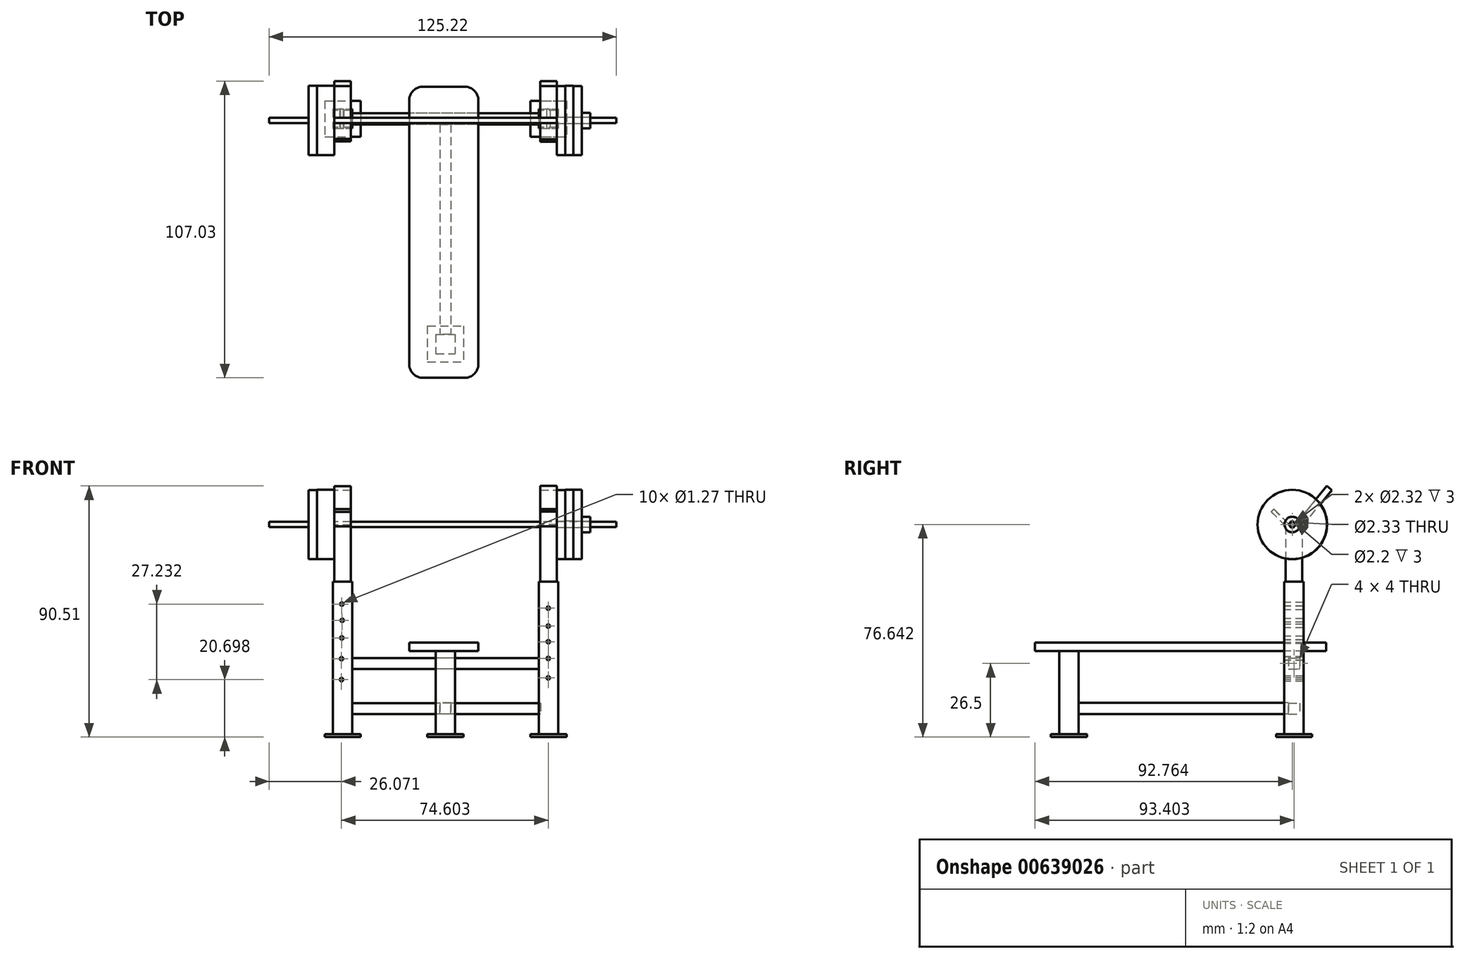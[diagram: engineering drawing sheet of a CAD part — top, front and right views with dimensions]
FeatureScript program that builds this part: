
annotation { "Feature Type Name" : "Feature", "Feature Type Description" : "" }
export const myFeature = defineFeature(function(context is Context, id is Id, definition is map)
    precondition{}
    {
        {
            var Q0;
            Q0=qCreatedBy(makeId("Top.planeOp"),FACE);
            var sketch = newSketch(context, id + "F0", { "sketchPlane" : qUnion([Q0])});
            skLineSegment(sketch, "E0.bottom", {"start": v(-45.73, 47.1) * mm, "end": v(-32.73, 47.1) * mm});
            skLineSegment(sketch, "E0.top", {"start": v(-45.73, 34.1) * mm, "end": v(-32.73, 34.1) * mm});
            skLineSegment(sketch, "E0.left", {"start": v(-45.73, 47.1) * mm, "end": v(-45.73, 34.1) * mm});
            skLineSegment(sketch, "E0.right", {"start": v(-32.73, 47.1) * mm, "end": v(-32.73, 34.1) * mm});
            skLineSegment(sketch, "E1.bottom", {"start": v(28.55, 47.1) * mm, "end": v(41.55, 47.1) * mm});
            skLineSegment(sketch, "E1.top", {"start": v(28.55, 34.1) * mm, "end": v(41.55, 34.1) * mm});
            skLineSegment(sketch, "E1.left", {"start": v(28.55, 47.1) * mm, "end": v(28.55, 34.1) * mm});
            skLineSegment(sketch, "E1.right", {"start": v(41.55, 47.1) * mm, "end": v(41.55, 34.1) * mm});
            skLineSegment(sketch, "E2.bottom", {"start": v(-8.67, -34.08) * mm, "end": v(4.33, -34.08) * mm});
            skLineSegment(sketch, "E2.top", {"start": v(-8.67, -47.08) * mm, "end": v(4.33, -47.08) * mm});
            skLineSegment(sketch, "E2.left", {"start": v(-8.67, -34.08) * mm, "end": v(-8.67, -47.08) * mm});
            skLineSegment(sketch, "E2.right", {"start": v(4.33, -34.08) * mm, "end": v(4.33, -47.08) * mm});
            skSolve(sketch);
        }
        {
            var Q0;
            Q0 = qSketchRegion(id + "F0", true);
            extrude(context, id + "F1", {"entities" : qUnion([Q0]), "depth" : 1 * mm, "offsetDistance" : 25.4 * mm});
        }
        {
            var Q0;
            Q0=makeQuery(id+"F1.opExtrude","CAP_FACE",FACE,{"disambiguationData":[OSD([sQuery(id+"F0.wireOp",EDGE,"E0.bottom"),sQuery(id+"F0.wireOp",EDGE,"E0.top"),sQuery(id+"F0.wireOp",EDGE,"E0.left"),sQuery(id+"F0.wireOp",EDGE,"E0.right")])],"isStart":false});
            var sketch = newSketch(context, id + "F2", { "sketchPlane" : qUnion([Q0])});
            skLineSegment(sketch, "E3.bottom", {"start": v(-42.73, 44.1) * mm, "end": v(-35.73, 44.1) * mm});
            skLineSegment(sketch, "E3.top", {"start": v(-42.73, 37.1) * mm, "end": v(-35.73, 37.1) * mm});
            skLineSegment(sketch, "E3.left", {"start": v(-42.73, 44.1) * mm, "end": v(-42.73, 37.1) * mm});
            skLineSegment(sketch, "E3.right", {"start": v(-35.73, 44.1) * mm, "end": v(-35.73, 37.1) * mm});
            skSolve(sketch);
        }
        {
            var Q0;
            Q0 = qSketchRegion(id + "F2", true);
            extrude(context, id + "F3", {"entities" : qUnion([Q0]), "operationType" : NewBodyOperationType.ADD, "depth" : 55 * mm, "offsetDistance" : 25.4 * mm});
        }
        {
            var Q0;
            Q0=makeQuery(id+"F1.opExtrude","CAP_FACE",FACE,{"disambiguationData":[OSD([sQuery(id+"F0.wireOp",EDGE,"E1.bottom"),sQuery(id+"F0.wireOp",EDGE,"E1.top"),sQuery(id+"F0.wireOp",EDGE,"E1.left"),sQuery(id+"F0.wireOp",EDGE,"E1.right")])],"isStart":false});
            var sketch = newSketch(context, id + "F4", { "sketchPlane" : qUnion([Q0])});
            skLineSegment(sketch, "E4.bottom", {"start": v(31.55, 44.1) * mm, "end": v(38.55, 44.1) * mm});
            skLineSegment(sketch, "E4.top", {"start": v(31.55, 37.1) * mm, "end": v(38.55, 37.1) * mm});
            skLineSegment(sketch, "E4.left", {"start": v(31.55, 44.1) * mm, "end": v(31.55, 37.1) * mm});
            skLineSegment(sketch, "E4.right", {"start": v(38.55, 44.1) * mm, "end": v(38.55, 37.1) * mm});
            skSolve(sketch);
        }
        {
            var Q0;
            Q0 = qSketchRegion(id + "F4", true);
            extrude(context, id + "F5", {"entities" : qUnion([Q0]), "operationType" : NewBodyOperationType.ADD, "depth" : 55 * mm, "offsetDistance" : 25.4 * mm});
        }
        {
            var Q0;
            Q0=makeQuery(id+"F1.opExtrude","CAP_FACE",FACE,{"disambiguationData":[OSD([sQuery(id+"F0.wireOp",EDGE,"E2.bottom"),sQuery(id+"F0.wireOp",EDGE,"E2.top"),sQuery(id+"F0.wireOp",EDGE,"E2.left"),sQuery(id+"F0.wireOp",EDGE,"E2.right")])],"isStart":false});
            var sketch = newSketch(context, id + "F6", { "sketchPlane" : qUnion([Q0])});
            skLineSegment(sketch, "E5.bottom", {"start": v(-5.67, -37.08) * mm, "end": v(1.33, -37.08) * mm});
            skLineSegment(sketch, "E5.top", {"start": v(-5.67, -44.08) * mm, "end": v(1.33, -44.08) * mm});
            skLineSegment(sketch, "E5.left", {"start": v(-5.67, -37.08) * mm, "end": v(-5.67, -44.08) * mm});
            skLineSegment(sketch, "E5.right", {"start": v(1.33, -37.08) * mm, "end": v(1.33, -44.08) * mm});
            skSolve(sketch);
        }
        {
            var Q0;
            Q0 = qSketchRegion(id + "F6", true);
            extrude(context, id + "F7", {"entities" : qUnion([Q0]), "operationType" : NewBodyOperationType.ADD, "depth" : 30 * mm, "offsetDistance" : 25.4 * mm});
        }
        {
            var Q0;
            Q0=makeQuery(id+"F3.opExtrude","SWEPT_FACE",FACE,{"disambiguationData":[OSD([sQuery(id+"F2.wireOp",EDGE,"E3.right")])]});
            var sketch = newSketch(context, id + "F8", { "sketchPlane" : qUnion([Q0])});
            skLineSegment(sketch, "E6.bottom", {"start": v(38.6, 12.27) * mm, "end": v(42.6, 12.27) * mm});
            skLineSegment(sketch, "E6.top", {"start": v(38.6, 8.27) * mm, "end": v(42.6, 8.27) * mm});
            skLineSegment(sketch, "E6.left", {"start": v(38.6, 12.27) * mm, "end": v(38.6, 8.27) * mm});
            skLineSegment(sketch, "E6.right", {"start": v(42.6, 12.27) * mm, "end": v(42.6, 8.27) * mm});
            skSolve(sketch);
        }
        {
            var Q0;
            Q0 = qSketchRegion(id + "F8", true);
            extrude(context, id + "F9", {"entities" : qUnion([Q0]), "depth" : 67.92 * mm, "offsetDistance" : 25.4 * mm});
        }
        {
            var Q0;
            Q0=makeQuery(id+"F3.opExtrude","SWEPT_FACE",FACE,{"disambiguationData":[OSD([sQuery(id+"F2.wireOp",EDGE,"E3.right")])]});
            var sketch = newSketch(context, id + "F10", { "sketchPlane" : qUnion([Q0])});
            skPoint(sketch, "E7.firstSnap0", {"position": v(37.1, 28.5) * mm});
            skLineSegment(sketch, "E7.bottom", {"start": v(38.6, 28.5) * mm, "end": v(42.6, 28.5) * mm});
            skLineSegment(sketch, "E7.top", {"start": v(38.6, 24.5) * mm, "end": v(42.6, 24.5) * mm});
            skLineSegment(sketch, "E7.left", {"start": v(38.6, 28.5) * mm, "end": v(38.6, 24.5) * mm});
            skLineSegment(sketch, "E7.right", {"start": v(42.6, 28.5) * mm, "end": v(42.6, 24.5) * mm});
            skSolve(sketch);
        }
        {
            var Q0;
            Q0 = qSketchRegion(id + "F10", true);
            extrude(context, id + "F11", {"entities" : qUnion([Q0]), "operationType" : NewBodyOperationType.ADD, "depth" : 67.82 * mm, "offsetDistance" : 25.4 * mm});
        }
        {
            var Q0;
            Q0=makeQuery(id+"F7.opExtrude","SWEPT_FACE",FACE,{"disambiguationData":[OSD([sQuery(id+"F6.wireOp",EDGE,"E5.bottom")])]});
            var sketch = newSketch(context, id + "F12", { "sketchPlane" : qUnion([Q0])});
            skLineSegment(sketch, "E8.bottom", {"start": v(0.17, 12.32) * mm, "end": v(4.17, 12.32) * mm});
            skLineSegment(sketch, "E8.top", {"start": v(0.17, 8.32) * mm, "end": v(4.17, 8.32) * mm});
            skLineSegment(sketch, "E8.left", {"start": v(0.17, 12.32) * mm, "end": v(0.17, 8.32) * mm});
            skLineSegment(sketch, "E8.right", {"start": v(4.17, 12.32) * mm, "end": v(4.17, 8.32) * mm});
            skSolve(sketch);
        }
        {
            var Q0;
            Q0 = qSketchRegion(id + "F12", true);
            extrude(context, id + "F13", {"entities" : qUnion([Q0]), "operationType" : NewBodyOperationType.ADD, "depth" : 75.72 * mm, "offsetDistance" : 25.4 * mm});
        }
        {
            var Q0;
            Q0=makeQuery(id+"F7.opExtrude","CAP_FACE",FACE,{"disambiguationData":[OSD([sQuery(id+"F6.wireOp",EDGE,"E5.bottom"),sQuery(id+"F6.wireOp",EDGE,"E5.top"),sQuery(id+"F6.wireOp",EDGE,"E5.left"),sQuery(id+"F6.wireOp",EDGE,"E5.right")])],"isStart":false});
            cPlane(context, id + "F14", {"entities" : qUnion([Q0]), "cplaneType" : CPlaneType.OFFSET, "offset" : 0 * mm, "width" : 152.4 * mm, "height" : 152.4 * mm});
        }
        {
            var Q0;
            Q0=qCreatedBy(id+"F14.planeOp",FACE);
            var sketch = newSketch(context, id + "F15", { "sketchPlane" : qUnion([Q0])});
            skLineSegment(sketch, "E9.bottom", {"start": v(9.77, 52.19) * mm, "end": v(-15.23, 52.19) * mm});
            skLineSegment(sketch, "E9.top", {"start": v(9.77, -52.81) * mm, "end": v(-15.23, -52.81) * mm});
            skLineSegment(sketch, "E9.left", {"start": v(9.77, 52.19) * mm, "end": v(9.77, -52.81) * mm});
            skLineSegment(sketch, "E9.right", {"start": v(-15.23, 52.19) * mm, "end": v(-15.23, -52.81) * mm});
            skSolve(sketch);
        }
        {
            var Q0;
            Q0 = qSketchRegion(id + "F15", true);
            extrude(context, id + "F16", {"entities" : qUnion([Q0]), "depth" : 3 * mm, "offsetDistance" : 25.4 * mm});
        }
        {
            var Q0;
            Q0=makeQuery(id+"F16.opExtrude","SWEPT_EDGE",EDGE,{"disambiguationData":[OSD([sQuery(id+"F15.wireOp",EDGE,"E9.bottom"),sQuery(id+"F15.wireOp",EDGE,"E9.right")])]});
            var Q1;
            Q1=makeQuery(id+"F16.opExtrude","SWEPT_EDGE",EDGE,{"disambiguationData":[OSD([sQuery(id+"F15.wireOp",EDGE,"E9.top"),sQuery(id+"F15.wireOp",EDGE,"E9.right")])]});
            var Q2;
            Q2=makeQuery(id+"F16.opExtrude","SWEPT_EDGE",EDGE,{"disambiguationData":[OSD([sQuery(id+"F15.wireOp",EDGE,"E9.top"),sQuery(id+"F15.wireOp",EDGE,"E9.left")])]});
            var Q3;
            Q3=makeQuery(id+"F16.opExtrude","SWEPT_EDGE",EDGE,{"disambiguationData":[OSD([sQuery(id+"F15.wireOp",EDGE,"E9.bottom"),sQuery(id+"F15.wireOp",EDGE,"E9.left")])]});
            fillet(context, id + "F17", {"entities" : qUnion([Q0, Q1, Q2, Q3]), "radius" : 5.08 * mm, "tangentPropagation" : true, "allowEdgeOverflow" : false});
        }
        {
            var Q0;
            Q0=makeQuery(id+"F3.opExtrude","CAP_FACE",FACE,{"disambiguationData":[OSD([sQuery(id+"F2.wireOp",EDGE,"E3.bottom"),sQuery(id+"F2.wireOp",EDGE,"E3.top"),sQuery(id+"F2.wireOp",EDGE,"E3.left"),sQuery(id+"F2.wireOp",EDGE,"E3.right")])],"isStart":false});
            var sketch = newSketch(context, id + "F18", { "sketchPlane" : qUnion([Q0])});
            skLineSegment(sketch, "E10.bottom", {"start": v(-36.23, 43.6) * mm, "end": v(-42.23, 43.6) * mm});
            skLineSegment(sketch, "E10.top", {"start": v(-36.23, 37.6) * mm, "end": v(-42.23, 37.6) * mm});
            skLineSegment(sketch, "E10.left", {"start": v(-36.23, 43.6) * mm, "end": v(-36.23, 37.6) * mm});
            skLineSegment(sketch, "E10.right", {"start": v(-42.23, 43.6) * mm, "end": v(-42.23, 37.6) * mm});
            skSolve(sketch);
        }
        {
            var Q0;
            Q0 = qSketchRegion(id + "F18", true);
            extrude(context, id + "F19", {"entities" : qUnion([Q0]), "operationType" : NewBodyOperationType.ADD, "depth" : 20 * mm, "offsetDistance" : 25.4 * mm});
        }
        {
            var Q0;
            Q0=makeQuery(id+"F5.opExtrude","CAP_FACE",FACE,{"disambiguationData":[OSD([sQuery(id+"F4.wireOp",EDGE,"E4.bottom"),sQuery(id+"F4.wireOp",EDGE,"E4.top"),sQuery(id+"F4.wireOp",EDGE,"E4.left"),sQuery(id+"F4.wireOp",EDGE,"E4.right")])],"isStart":false});
            var sketch = newSketch(context, id + "F20", { "sketchPlane" : qUnion([Q0])});
            skLineSegment(sketch, "E11.bottom", {"start": v(38.05, 37.6) * mm, "end": v(32.05, 37.6) * mm});
            skLineSegment(sketch, "E11.top", {"start": v(38.05, 43.6) * mm, "end": v(32.05, 43.6) * mm});
            skLineSegment(sketch, "E11.left", {"start": v(38.05, 37.6) * mm, "end": v(38.05, 43.6) * mm});
            skLineSegment(sketch, "E11.right", {"start": v(32.05, 37.6) * mm, "end": v(32.05, 43.6) * mm});
            skSolve(sketch);
        }
        {
            var Q0;
            Q0 = qSketchRegion(id + "F20", true);
            extrude(context, id + "F21", {"entities" : qUnion([Q0]), "operationType" : NewBodyOperationType.ADD, "depth" : 20 * mm, "offsetDistance" : 25.4 * mm});
        }
        {
            var Q0;
            Q0=makeQuery(id+"F21.opExtrude","SWEPT_FACE",FACE,{"disambiguationData":[OSD([sQuery(id+"F20.wireOp",EDGE,"E11.left")])]});
            var sketch = newSketch(context, id + "F22", { "sketchPlane" : qUnion([Q0])});
            skLineSegment(sketch, "E12", {"start": v(37.6, 76) * mm, "end": v(32.31, 81.3) * mm});
            skLineSegment(sketch, "E13", {"start": v(32.31, 81.3) * mm, "end": v(33.22, 82.2) * mm});
            skLineSegment(sketch, "E14", {"start": v(33.22, 82.2) * mm, "end": v(39.4, 76) * mm});
            skLineSegment(sketch, "E15", {"start": v(39.4, 76) * mm, "end": v(37.6, 76) * mm});
            skSolve(sketch);
        }
        {
            var Q0;
            Q0 = qSketchRegion(id + "F22", true);
            extrude(context, id + "F23", {"entities" : qUnion([Q0]), "operationType" : NewBodyOperationType.ADD, "oppositeDirection" : true, "depth" : 6 * mm, "offsetDistance" : 25.4 * mm});
        }
        {
            var Q0;
            Q0=makeQuery(id+"F23.boolean.opBoolean","MERGE",FACE,{"derivedFrom":[makeQuery(id+"F21.opExtrude","SWEPT_FACE",FACE,{"disambiguationData":[OSD([sQuery(id+"F20.wireOp",EDGE,"E11.left")])]}),makeQuery(id+"F23.opExtrude","CAP_FACE",FACE,{"disambiguationData":[OSD([sQuery(id+"F22.wireOp",EDGE,"E12"),sQuery(id+"F22.wireOp",EDGE,"E13"),sQuery(id+"F22.wireOp",EDGE,"E14"),sQuery(id+"F22.wireOp",EDGE,"E15")])],"isStart":true})]});
            var sketch = newSketch(context, id + "F24", { "sketchPlane" : qUnion([Q0])});
            skLineSegment(sketch, "E16", {"start": v(43.6, 76) * mm, "end": v(54.22, 89) * mm});
            skLineSegment(sketch, "E17", {"start": v(54.22, 89) * mm, "end": v(52.37, 90.5) * mm});
            skLineSegment(sketch, "E18", {"start": v(52.37, 90.5) * mm, "end": v(40.51, 76) * mm});
            skPoint(sketch, "E18.endSnap0", {"position": v(41.5, 76) * mm});
            skLineSegment(sketch, "E19", {"start": v(40.51, 76) * mm, "end": v(43.6, 76) * mm});
            skSolve(sketch);
        }
        {
            var Q0;
            Q0 = qSketchRegion(id + "F24", true);
            extrude(context, id + "F25", {"entities" : qUnion([Q0]), "operationType" : NewBodyOperationType.ADD, "oppositeDirection" : true, "depth" : 6 * mm, "offsetDistance" : 25.4 * mm});
        }
        {
            var Q0;
            Q0=makeQuery(id+"F19.opExtrude","SWEPT_FACE",FACE,{"disambiguationData":[OSD([sQuery(id+"F18.wireOp",EDGE,"E10.right")])]});
            var sketch = newSketch(context, id + "F26", { "sketchPlane" : qUnion([Q0])});
            skLineSegment(sketch, "E20", {"start": v(-37.6, 76) * mm, "end": v(-32.41, 81.17) * mm});
            skLineSegment(sketch, "E21", {"start": v(-32.41, 81.17) * mm, "end": v(-33.37, 82.13) * mm});
            skLineSegment(sketch, "E22", {"start": v(-33.37, 82.13) * mm, "end": v(-39.51, 76) * mm});
            skLineSegment(sketch, "E23", {"start": v(-39.51, 76) * mm, "end": v(-37.6, 76) * mm});
            skLineSegment(sketch, "E24", {"start": v(-43.6, 76) * mm, "end": v(-54.18, 88.94) * mm});
            skLineSegment(sketch, "E25", {"start": v(-54.18, 88.94) * mm, "end": v(-52.34, 90.44) * mm});
            skLineSegment(sketch, "E26", {"start": v(-52.34, 90.44) * mm, "end": v(-40.53, 76) * mm});
            skLineSegment(sketch, "E27", {"start": v(-40.53, 76) * mm, "end": v(-43.6, 76) * mm});
            skSolve(sketch);
        }
        {
            var Q0;
            Q0 = qSketchRegion(id + "F26", true);
            extrude(context, id + "F27", {"entities" : qUnion([Q0]), "operationType" : NewBodyOperationType.ADD, "oppositeDirection" : true, "depth" : 6 * mm, "offsetDistance" : 25.4 * mm});
        }
        {
            var Q0;
            Q0=makeQuery(id+"F27.boolean.opBoolean","MERGE",FACE,{"derivedFrom":[makeQuery(id+"F19.opExtrude","SWEPT_FACE",FACE,{"disambiguationData":[OSD([sQuery(id+"F18.wireOp",EDGE,"E10.right")])]}),makeQuery(id+"F27.opExtrude","CAP_FACE",FACE,{"disambiguationData":[OSD([sQuery(id+"F26.wireOp",EDGE,"E20"),sQuery(id+"F26.wireOp",EDGE,"E21"),sQuery(id+"F26.wireOp",EDGE,"E22"),sQuery(id+"F26.wireOp",EDGE,"E23")])],"isStart":true}),makeQuery(id+"F27.opExtrude","CAP_FACE",FACE,{"disambiguationData":[OSD([sQuery(id+"F26.wireOp",EDGE,"E24"),sQuery(id+"F26.wireOp",EDGE,"E25"),sQuery(id+"F26.wireOp",EDGE,"E26"),sQuery(id+"F26.wireOp",EDGE,"E27")])],"isStart":true})]});
            var sketch = newSketch(context, id + "F28", { "sketchPlane" : qUnion([Q0])});
            skCircle(sketch, "E28", {"center": v(-40.02, 76.62) * mm, "radius": 12.5 * mm});
            skPoint(sketch, "E28.centerSnap0", {"position": v(-40.02, 76) * mm});
            skSolve(sketch);
        }
        {
            var Q0;
            Q0 = qSketchRegion(id + "F28", true);
            extrude(context, id + "F29", {"entities" : qUnion([Q0]), "operationType" : NewBodyOperationType.ADD, "depth" : 3.17 * mm, "offsetDistance" : 25.4 * mm});
        }
        {
            var Q0;
            Q0=makeQuery(id+"F29.opExtrude","CAP_FACE",FACE,{"disambiguationData":[OSD([sQuery(id+"F28.wireOp",EDGE,"E28")])],"isStart":false});
            var sketch = newSketch(context, id + "F30", { "sketchPlane" : qUnion([Q0])});
            skCircle(sketch, "E29", {"center": v(-40.02, 76.62) * mm, "radius": 12.5 * mm});
            skSolve(sketch);
        }
        {
            var Q0;
            Q0 = qSketchRegion(id + "F30", true);
            extrude(context, id + "F31", {"entities" : qUnion([Q0]), "operationType" : NewBodyOperationType.ADD, "depth" : 3.05 * mm, "offsetDistance" : 25.4 * mm});
        }
        {
            var Q0;
            Q0=makeQuery(id+"F31.opExtrude","CAP_FACE",FACE,{"disambiguationData":[OSD([sQuery(id+"F30.wireOp",EDGE,"E29")])],"isStart":false});
            var sketch = newSketch(context, id + "F32", { "sketchPlane" : qUnion([Q0])});
            skCircle(sketch, "E30", {"center": v(-40.02, 76.62) * mm, "radius": 12.48 * mm});
            skSolve(sketch);
        }
        {
            var Q0;
            Q0 = qSketchRegion(id + "F32", true);
            extrude(context, id + "F33", {"entities" : qUnion([Q0]), "operationType" : NewBodyOperationType.ADD, "depth" : 3.05 * mm, "offsetDistance" : 25.4 * mm});
        }
        {
            var Q0;
            Q0=makeQuery(id+"F33.opExtrude","CAP_FACE",FACE,{"disambiguationData":[OSD([sQuery(id+"F32.wireOp",EDGE,"E30")])],"isStart":false});
            var sketch = newSketch(context, id + "F34", { "sketchPlane" : qUnion([Q0])});
            skCircle(sketch, "E31", {"center": v(-40.02, 76.62) * mm, "radius": 0.95 * mm});
            skSolve(sketch);
        }
        {
            var Q0;
            Q0 = qSketchRegion(id + "F34", true);
            extrude(context, id + "F35", {"entities" : qUnion([Q0]), "operationType" : NewBodyOperationType.ADD, "oppositeDirection" : true, "depth" : 111 * mm, "offsetDistance" : 25.4 * mm, "hasSecondDirection" : true, "secondDirectionOppositeDirection" : false, "secondDirectionDepth" : 14.22 * mm});
        }
        {
            var Q0;
            Q0=makeQuery(id+"F25.boolean.opBoolean","MERGE",FACE,{"derivedFrom":[makeQuery(id+"F23.boolean.opBoolean","MERGE",FACE,{"derivedFrom":[makeQuery(id+"F21.opExtrude","SWEPT_FACE",FACE,{"disambiguationData":[OSD([sQuery(id+"F20.wireOp",EDGE,"E11.left")])]}),makeQuery(id+"F23.opExtrude","CAP_FACE",FACE,{"disambiguationData":[OSD([sQuery(id+"F22.wireOp",EDGE,"E12"),sQuery(id+"F22.wireOp",EDGE,"E13"),sQuery(id+"F22.wireOp",EDGE,"E14"),sQuery(id+"F22.wireOp",EDGE,"E15")])],"isStart":true})]}),makeQuery(id+"F25.opExtrude","CAP_FACE",FACE,{"disambiguationData":[OSD([sQuery(id+"F24.wireOp",EDGE,"E16"),sQuery(id+"F24.wireOp",EDGE,"E17"),sQuery(id+"F24.wireOp",EDGE,"E18"),sQuery(id+"F24.wireOp",EDGE,"E19")])],"isStart":true})]});
            var sketch = newSketch(context, id + "F36", { "sketchPlane" : qUnion([Q0])});
            skCircle(sketch, "E32", {"center": v(39.95, 76.64) * mm, "radius": 12.44 * mm});
            skPoint(sketch, "E32.centerSnap0", {"position": v(39.95, 76) * mm});
            skCircle(sketch, "E33", {"center": v(39.95, 76.64) * mm, "radius": 1.16 * mm});
            skSolve(sketch);
        }
        {
            var Q0;
            Q0 = qSketchRegion(id + "F36", true);
            extrude(context, id + "F37", {"entities" : qUnion([Q0]), "operationType" : NewBodyOperationType.ADD, "depth" : 3 * mm, "offsetDistance" : 25.4 * mm});
        }
        {
            var Q0;
            Q0=makeQuery(id+"F37.opExtrude","CAP_FACE",FACE,{"disambiguationData":[OSD([sQuery(id+"F36.wireOp",EDGE,"E32"),sQuery(id+"F36.wireOp",EDGE,"E33")])],"isStart":false});
            var sketch = newSketch(context, id + "F38", { "sketchPlane" : qUnion([Q0])});
            skCircle(sketch, "E34", {"center": v(39.95, 76.64) * mm, "radius": 12.51 * mm});
            skCircle(sketch, "E35", {"center": v(39.95, 76.64) * mm, "radius": 1.16 * mm});
            skSolve(sketch);
        }
        {
            var Q0;
            Q0 = qSketchRegion(id + "F38", true);
            extrude(context, id + "F39", {"entities" : qUnion([Q0]), "operationType" : NewBodyOperationType.ADD, "depth" : 3 * mm, "offsetDistance" : 25.4 * mm});
        }
        {
            var Q0;
            Q0=makeQuery(id+"F39.opExtrude","CAP_FACE",FACE,{"disambiguationData":[OSD([sQuery(id+"F38.wireOp",EDGE,"E34"),sQuery(id+"F38.wireOp",EDGE,"E35")])],"isStart":false});
            var sketch = newSketch(context, id + "F40", { "sketchPlane" : qUnion([Q0])});
            skCircle(sketch, "E36", {"center": v(39.95, 76.64) * mm, "radius": 12.5 * mm});
            skCircle(sketch, "E37", {"center": v(39.95, 76.64) * mm, "radius": 1.16 * mm});
            skSolve(sketch);
        }
        {
            var Q0;
            Q0 = qSketchRegion(id + "F40", true);
            extrude(context, id + "F41", {"entities" : qUnion([Q0]), "operationType" : NewBodyOperationType.ADD, "depth" : 3 * mm, "offsetDistance" : 25.4 * mm});
        }
        {
            var Q0;
            Q0=makeQuery(id+"F41.opExtrude","CAP_FACE",FACE,{"disambiguationData":[OSD([sQuery(id+"F40.wireOp",EDGE,"E36"),sQuery(id+"F40.wireOp",EDGE,"E37")])],"isStart":false});
            var sketch = newSketch(context, id + "F42", { "sketchPlane" : qUnion([Q0])});
            skCircle(sketch, "E38", {"center": v(39.95, 76.64) * mm, "radius": 2.8 * mm});
            skCircle(sketch, "E39", {"center": v(39.95, 76.64) * mm, "radius": 1.1 * mm});
            skSolve(sketch);
        }
        {
            var Q0;
            Q0 = qSketchRegion(id + "F42", true);
            extrude(context, id + "F43", {"entities" : qUnion([Q0]), "operationType" : NewBodyOperationType.ADD, "depth" : 3 * mm, "offsetDistance" : 25.4 * mm});
        }
        {
            var Q0;
            Q0=makeQuery(id+"F5.opExtrude","SWEPT_FACE",FACE,{"disambiguationData":[OSD([sQuery(id+"F4.wireOp",EDGE,"E4.top")])]});
            var sketch = newSketch(context, id + "F44", { "sketchPlane" : qUnion([Q0])});
            skCircle(sketch, "E40", {"center": v(34.95, 46.48) * mm, "radius": 0.64 * mm});
            skCircle(sketch, "E41", {"center": v(34.95, 40.01) * mm, "radius": 0.64 * mm});
            skCircle(sketch, "E42", {"center": v(34.95, 34.35) * mm, "radius": 0.64 * mm});
            skCircle(sketch, "E43", {"center": v(34.95, 28.34) * mm, "radius": 0.64 * mm});
            skCircle(sketch, "E44", {"center": v(34.95, 21.33) * mm, "radius": 0.64 * mm});
            skSolve(sketch);
        }
        {
            var Q0;
            Q0 = qSketchRegion(id + "F44", true);
            extrude(context, id + "F45", {"entities" : qUnion([Q0]), "operationType" : NewBodyOperationType.REMOVE, "oppositeDirection" : true, "depth" : 7.37 * mm, "offsetDistance" : 25.4 * mm});
        }
        {
            var Q0;
            Q0=makeQuery(id+"F3.opExtrude","SWEPT_FACE",FACE,{"disambiguationData":[OSD([sQuery(id+"F2.wireOp",EDGE,"E3.top")])]});
            var sketch = newSketch(context, id + "F46", { "sketchPlane" : qUnion([Q0])});
            skCircle(sketch, "E45", {"center": v(-39.65, 20.7) * mm, "radius": 0.64 * mm});
            skCircle(sketch, "E46", {"center": v(-39.64, 28.24) * mm, "radius": 0.64 * mm});
            skCircle(sketch, "E47", {"center": v(-39.53, 35.72) * mm, "radius": 0.64 * mm});
            skCircle(sketch, "E48", {"center": v(-39.38, 42.09) * mm, "radius": 0.64 * mm});
            skCircle(sketch, "E49", {"center": v(-39.52, 47.93) * mm, "radius": 0.64 * mm});
            skSolve(sketch);
        }
        {
            var Q0;
            Q0 = qSketchRegion(id + "F46", true);
            extrude(context, id + "F47", {"entities" : qUnion([Q0]), "operationType" : NewBodyOperationType.REMOVE, "oppositeDirection" : true, "depth" : 25.4 * mm, "offsetDistance" : 25.4 * mm});
        }
    });
